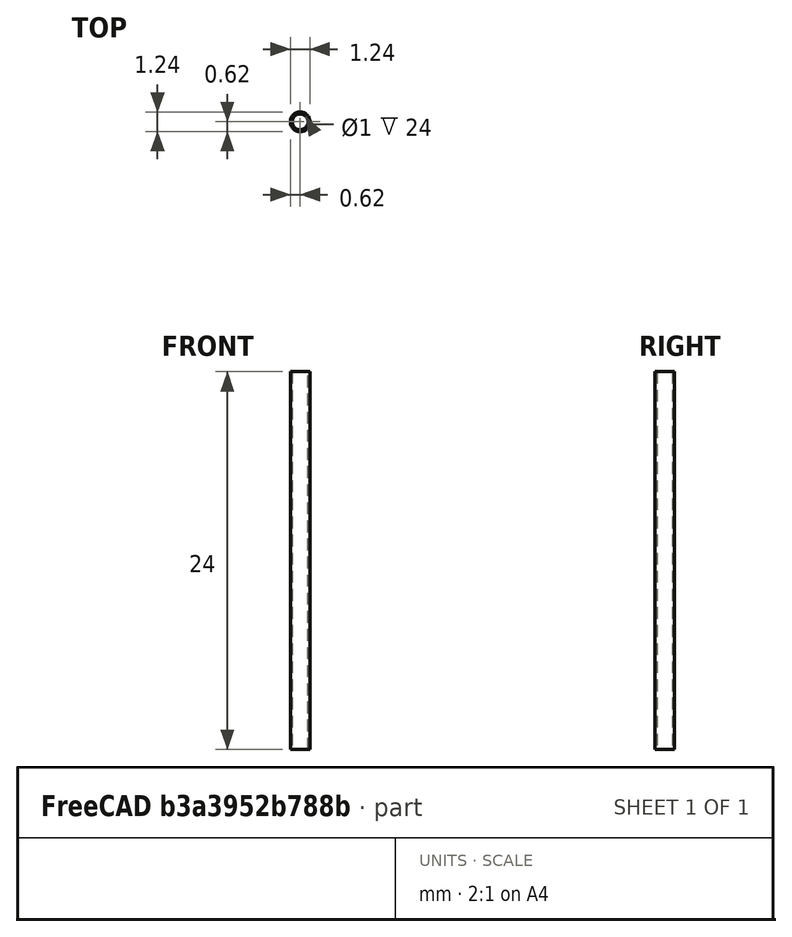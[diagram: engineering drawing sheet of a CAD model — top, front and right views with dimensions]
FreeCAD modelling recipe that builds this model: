
FCSTD DOCUMENT  (FreeCAD 0.21R33771 (Git))
Label: pipe
License: All rights reserved
LicenseURL: http://en.wikipedia.org/wiki/All_rights_reserved
objects: Part::Cylinder×2, Spreadsheet::Sheet×1, Part::Cut×1
note: 3 computed .brp shape members not serialized (recipe doc carries the construction recipe); baked Part::Feature solids carry a one-line shape summary decoded from their .brp

FEATURE [Part::Cylinder] Cylinder  label="base"
  Angle = 360
  AttacherType = Attacher::AttachEngine3D
  FirstAngle = 0
  Height = 24
  Radius = 0.625
  SecondAngle = 0
  expr: Height = <<ss>>.ss_len
  expr: Radius = <<ss>>.ss_id + <<ss>>.ss_wall
FEATURE [Part::Cylinder] Cylinder001  label="tool"
  Angle = 360
  AttacherType = Attacher::AttachEngine3D
  FirstAngle = 0
  Height = 24
  Radius = 0.5
  SecondAngle = 0
  expr: Height = <<ss>>.ss_len
  expr: Radius = <<ss>>.ss_id
FEATURE [Spreadsheet::Sheet] Spreadsheet  label="ss"
  cells = A2='ss_len; B2(ss_len)=24; A3='ss_rad; B3(ss_id)==1 / 2; A4='ss_wall; B4(ss_wall)==1 / 8
FEATURE [Part::Cut] Cut
  Base = -> Cylinder
  Tool = -> Cylinder001
